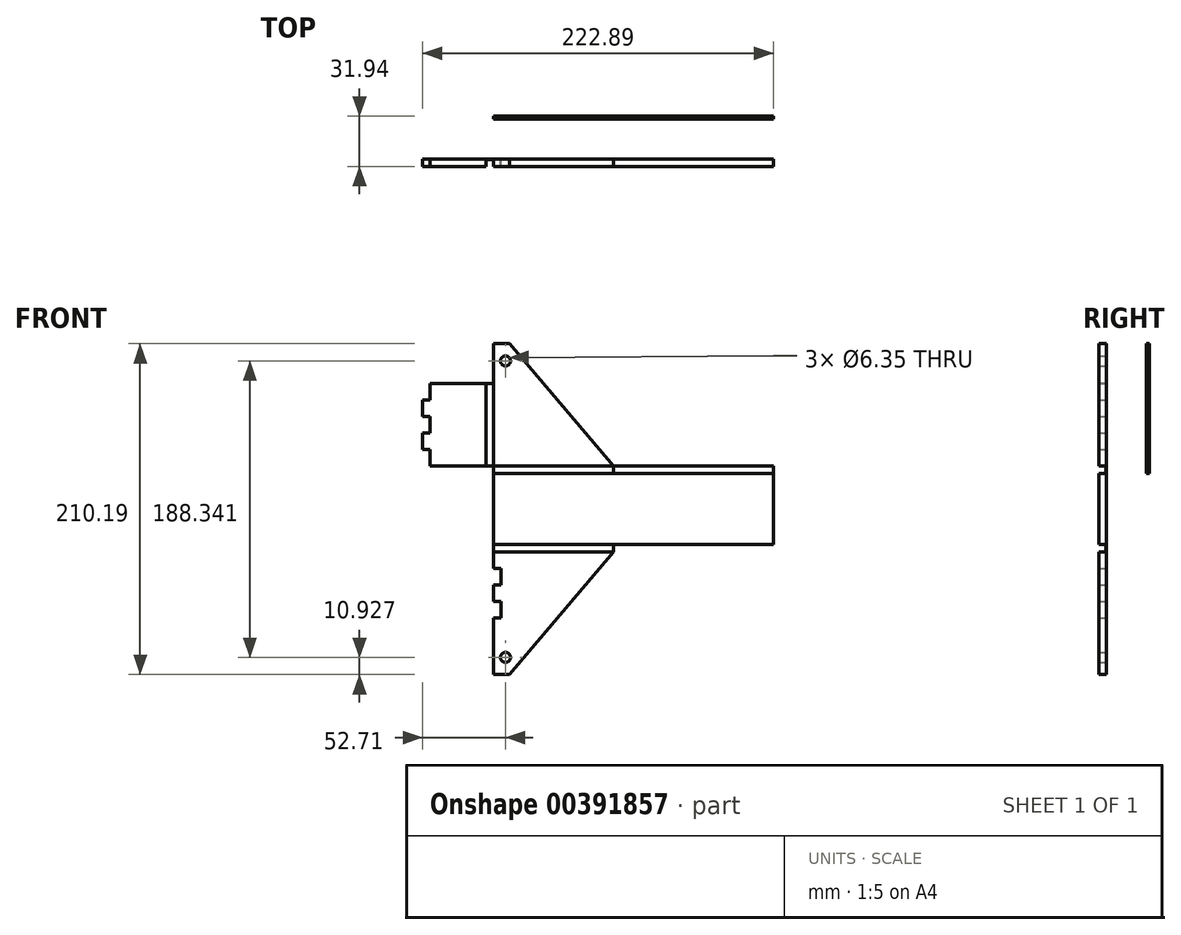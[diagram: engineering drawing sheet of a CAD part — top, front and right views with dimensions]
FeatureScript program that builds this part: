
annotation { "Feature Type Name" : "Feature", "Feature Type Description" : "" }
export const myFeature = defineFeature(function(context is Context, id is Id, definition is map)
    precondition{}
    {
        {
            var Q0;
            Q0=qCreatedBy(makeId("Front.planeOp"),FACE);
            var sketch = newSketch(context, id + "F0", { "sketchPlane" : qUnion([Q0])});
            skLineSegment(sketch, "E0.top", {"start": v(0, 0) * mm, "end": v(177.8, 0) * mm});
            skLineSegment(sketch, "E0.left", {"start": v(0, 82.55) * mm, "end": v(0, 0) * mm});
            skLineSegment(sketch, "E1", {"start": v(177.8, 0) * mm, "end": v(177.8, 4.76) * mm});
            skLineSegment(sketch, "E2", {"start": v(177.8, 4.76) * mm, "end": v(76.2, 4.76) * mm});
            skLineSegment(sketch, "E3", {"start": v(0, 82.55) * mm, "end": v(10.16, 82.55) * mm});
            skLineSegment(sketch, "E4", {"start": v(10.16, 82.55) * mm, "end": v(76.2, 4.76) * mm});
            skSolve(sketch);
        }
        {
            var Q0;
            Q0 = qSketchRegion(id + "F0", true);
            extrude(context, id + "F1", {"entities" : qUnion([Q0]), "depth" : (1.4 + (6 / 16)) * mm});
        }
        {
            var Q0;
            Q0=makeQuery(id+"F1.opExtrude","SWEPT_FACE",FACE,{"disambiguationData":[OSD([sQuery(id+"F0.wireOp",EDGE,"E3")])]});
            var sketch = newSketch(context, id + "F2", { "sketchPlane" : qUnion([Q0])});
            skLineSegment(sketch, "E5.bottom", {"start": v(4.76, -4.76) * mm, "end": v(76.2, -4.76) * mm});
            skLineSegment(sketch, "E5.top", {"start": v(4.76, -40.32) * mm, "end": v(76.2, -40.32) * mm});
            skLineSegment(sketch, "E5.left", {"start": v(4.76, -4.76) * mm, "end": v(4.76, -40.32) * mm});
            skLineSegment(sketch, "E5.right", {"start": v(76.2, -4.76) * mm, "end": v(76.2, -40.32) * mm});
            skSolve(sketch);
        }
        {
            var Q0;
            Q0 = qSketchRegion(id + "F2", true);
            var Q1;
            Q1=makeQuery(id+"F1.opExtrude","SWEPT_FACE",FACE,{"disambiguationData":[OSD([sQuery(id+"F0.wireOp",EDGE,"E2")])]});
            extrude(context, id + "F3", {"entities" : qUnion([Q0]), "operationType" : NewBodyOperationType.REMOVE, "endBound" : BoundingType.UP_TO_SURFACE, "oppositeDirection" : true, "endBoundEntityFace" : qUnion([Q1]), "depth" : 25.4 * mm});
        }
        {
            var Q0;
            Q0=makeQuery(id+"F1.opExtrude","CAP_FACE",FACE,{"disambiguationData":[OSD([sQuery(id+"F0.wireOp",EDGE,"E0.top"),sQuery(id+"F0.wireOp",EDGE,"E0.left"),sQuery(id+"F0.wireOp",EDGE,"E1"),sQuery(id+"F0.wireOp",EDGE,"E2"),sQuery(id+"F0.wireOp",EDGE,"adjmG31n-KMU0-T1bu-X0pq-MTYf4ImsonU8")])],"isStart":false});
            var sketch = newSketch(context, id + "F4", { "sketchPlane" : qUnion([Q0])});
            skCircle(sketch, "E6", {"center": v(7.62, 71.63) * mm, "radius": 3.18 * mm});
            skSolve(sketch);
        }
        {
            var Q0;
            Q0 = qSketchRegion(id + "F4", true);
            extrude(context, id + "F5", {"entities" : qUnion([Q0]), "operationType" : NewBodyOperationType.REMOVE, "endBound" : BoundingType.THROUGH_ALL, "oppositeDirection" : true, "depth" : 25.4 * mm});
        }
        {
            var Q0;
            Q0=makeQuery(id+"F1.opExtrude","SWEPT_FACE",FACE,{"disambiguationData":[OSD([sQuery(id+"F0.wireOp",EDGE,"E0.left")])]});
            var sketch = newSketch(context, id + "F6", { "sketchPlane" : qUnion([Q0])});
            skLineSegment(sketch, "E7.bottom", {"start": v(4.76, 82.55) * mm, "end": v(40.32, 82.55) * mm});
            skLineSegment(sketch, "E7.top", {"start": v(4.76, 57.15) * mm, "end": v(40.32, 57.15) * mm});
            skLineSegment(sketch, "E7.left", {"start": v(4.76, 82.55) * mm, "end": v(4.76, 57.15) * mm});
            skLineSegment(sketch, "E7.right", {"start": v(40.32, 82.55) * mm, "end": v(40.32, 57.15) * mm});
            skSolve(sketch);
        }
        {
            var Q0;
            Q0 = qSketchRegion(id + "F6", true);
            extrude(context, id + "F7", {"entities" : qUnion([Q0]), "operationType" : NewBodyOperationType.REMOVE, "endBound" : BoundingType.THROUGH_ALL, "oppositeDirection" : true, "depth" : 25.4 * mm});
        }
        {
            var Q0;
            Q0=makeQuery(id+"F1.opExtrude","CAP_FACE",FACE,{"disambiguationData":[OSD([sQuery(id+"F0.wireOp",EDGE,"E0.top"),sQuery(id+"F0.wireOp",EDGE,"E0.left"),sQuery(id+"F0.wireOp",EDGE,"E1"),sQuery(id+"F0.wireOp",EDGE,"E2"),sQuery(id+"F0.wireOp",EDGE,"E3"),sQuery(id+"F0.wireOp",EDGE,"E4")])],"isStart":false});
            cPlane(context, id + "F8", {"entities" : qUnion([Q0]), "cplaneType" : CPlaneType.OFFSET, "offset" : 25.4 * mm, "width" : 152.4 * mm, "height" : 152.4 * mm});
        }
        {
            var Q0;
            Q0=qCreatedBy(id+"F8.planeOp",FACE);
            var sketch = newSketch(context, id + "F9", { "sketchPlane" : qUnion([Q0])});
            skLineSegment(sketch, "E8", {"start": v(76.2, 4.76) * mm, "end": v(10.16, 82.55) * mm});
            skLineSegment(sketch, "E9", {"start": v(10.16, 82.55) * mm, "end": v(0, 82.55) * mm});
            skLineSegment(sketch, "E10", {"start": v(76.2, 4.76) * mm, "end": v(0, 4.76) * mm, "construction": true});
            skLineSegment(sketch, "E11", {"start": v(0, 4.76) * mm, "end": v(0, 57.15) * mm, "construction": true});
            skLineSegment(sketch, "E12", {"start": v(76.2, 4.76) * mm, "end": v(76.2, 0) * mm});
            skLineSegment(sketch, "E13", {"start": v(76.2, 0) * mm, "end": v(0, 0) * mm, "construction": true});
            skLineSegment(sketch, "E14", {"start": v(0, 0) * mm, "end": v(0, 4.76) * mm});
            skLineSegment(sketch, "E15", {"start": v(0, 0) * mm, "end": v(0, -45.08) * mm});
            skLineSegment(sketch, "E16", {"start": v(177.8, -45.09) * mm, "end": v(177.8, 0) * mm});
            skLineSegment(sketch, "E17", {"start": v(76.2, 0) * mm, "end": v(177.8, 0) * mm});
            skLineSegment(sketch, "E18", {"start": v(0, -22.54) * mm, "end": v(177.8, -22.54) * mm, "construction": true});
            skLineSegment(sketch, "E19.MirrorCS", {"start": v(76.2, -45.08) * mm, "end": v(177.8, -45.08) * mm});
            skLineSegment(sketch, "E20.MirrorCS", {"start": v(76.2, -45.08) * mm, "end": v(0, -45.08) * mm, "construction": true});
            skLineSegment(sketch, "E21.MirrorCS", {"start": v(0, -45.08) * mm, "end": v(0, -49.85) * mm});
            skLineSegment(sketch, "E22.MirrorCS", {"start": v(76.2, -49.85) * mm, "end": v(0, -49.85) * mm, "construction": true});
            skLineSegment(sketch, "E23.MirrorCS", {"start": v(76.2, -49.85) * mm, "end": v(10.16, -127.64) * mm});
            skLineSegment(sketch, "E24.MirrorCS", {"start": v(76.2, -49.85) * mm, "end": v(76.2, -45.08) * mm});
            skLineSegment(sketch, "E25.MirrorCS", {"start": v(10.16, -127.64) * mm, "end": v(0, -127.64) * mm});
            skLineSegment(sketch, "E26", {"start": v(0, 4.76) * mm, "end": v(-4.76, 4.76) * mm});
            skLineSegment(sketch, "E27", {"start": v(-4.76, 4.76) * mm, "end": v(-4.76, 57.15) * mm, "construction": true});
            skLineSegment(sketch, "E28", {"start": v(-4.76, 57.15) * mm, "end": v(0, 57.15) * mm});
            skLineSegment(sketch, "E29", {"start": v(-4.76, 4.76) * mm, "end": v(-40.32, 4.76) * mm});
            skLineSegment(sketch, "E30", {"start": v(-40.32, 57.15) * mm, "end": v(-4.76, 57.15) * mm});
            skLineSegment(sketch, "E31", {"start": v(-40.32, 4.76) * mm, "end": v(-45.08, 4.76) * mm, "construction": true});
            skLineSegment(sketch, "E32", {"start": v(-45.08, 57.15) * mm, "end": v(-40.32, 57.15) * mm, "construction": true});
            skLineSegment(sketch, "E33", {"start": v(-45.08, 57.15) * mm, "end": v(-45.08, 46.67) * mm, "construction": true});
            skLineSegment(sketch, "E34", {"start": v(-45.08, 46.67) * mm, "end": v(-45.08, 36.2) * mm});
            skLineSegment(sketch, "E35", {"start": v(-45.08, 36.2) * mm, "end": v(-45.08, 25.72) * mm, "construction": true});
            skLineSegment(sketch, "E36", {"start": v(-45.08, 25.72) * mm, "end": v(-45.08, 15.24) * mm});
            skLineSegment(sketch, "E37", {"start": v(-45.08, 15.24) * mm, "end": v(-45.08, 4.76) * mm, "construction": true});
            skLineSegment(sketch, "E38", {"start": v(-45.08, 46.67) * mm, "end": v(-40.32, 46.67) * mm});
            skLineSegment(sketch, "E39", {"start": v(-45.08, 36.2) * mm, "end": v(-40.32, 36.2) * mm});
            skLineSegment(sketch, "E40", {"start": v(-45.08, 25.72) * mm, "end": v(-40.32, 25.72) * mm});
            skLineSegment(sketch, "E41", {"start": v(-45.08, 15.24) * mm, "end": v(-40.32, 15.24) * mm});
            skLineSegment(sketch, "E42", {"start": v(-40.32, 57.15) * mm, "end": v(-40.32, 46.67) * mm});
            skLineSegment(sketch, "E43", {"start": v(-40.32, 36.2) * mm, "end": v(-40.32, 25.72) * mm});
            skLineSegment(sketch, "E44", {"start": v(-40.32, 15.24) * mm, "end": v(-40.32, 4.76) * mm});
            skLineSegment(sketch, "E45", {"start": v(-40.32, 15.24) * mm, "end": v(-40.32, 25.72) * mm, "construction": true});
            skLineSegment(sketch, "E46", {"start": v(-40.32, 36.2) * mm, "end": v(-40.32, 46.67) * mm, "construction": true});
            skLineSegment(sketch, "E47", {"start": v(0, -49.85) * mm, "end": v(0, -60.33) * mm});
            skLineSegment(sketch, "E48", {"start": v(0, -60.33) * mm, "end": v(0, -70.8) * mm, "construction": true});
            skLineSegment(sketch, "E49", {"start": v(0, -81.28) * mm, "end": v(0, -91.76) * mm, "construction": true});
            skLineSegment(sketch, "E50", {"start": v(0, -91.76) * mm, "end": v(0, -102.23) * mm});
            skLineSegment(sketch, "E51", {"start": v(0, -102.23) * mm, "end": v(0, -127.64) * mm});
            skLineSegment(sketch, "E52", {"start": v(0, 57.15) * mm, "end": v(0, 82.55) * mm});
            skLineSegment(sketch, "E53", {"start": v(0, -70.8) * mm, "end": v(0, -81.28) * mm});
            skLineSegment(sketch, "E54", {"start": v(0, -60.33) * mm, "end": v(4.76, -60.33) * mm});
            skLineSegment(sketch, "E55", {"start": v(4.76, -60.33) * mm, "end": v(4.76, -70.8) * mm});
            skLineSegment(sketch, "E56", {"start": v(4.76, -70.8) * mm, "end": v(0, -70.8) * mm});
            skLineSegment(sketch, "E57", {"start": v(0, -81.28) * mm, "end": v(4.76, -81.28) * mm});
            skLineSegment(sketch, "E58", {"start": v(4.76, -81.28) * mm, "end": v(4.76, -91.76) * mm});
            skLineSegment(sketch, "E59", {"start": v(4.76, -91.76) * mm, "end": v(0, -91.76) * mm});
            skCircle(sketch, "E60", {"center": v(7.62, 71.63) * mm, "radius": 3.18 * mm});
            skCircle(sketch, "E61.MirrorC", {"center": v(7.62, -116.71) * mm, "radius": 3.18 * mm});
            skLineSegment(sketch, "E62", {"start": v(-45.08, 51.91) * mm, "end": v(0, 51.91) * mm, "construction": true});
            skSolve(sketch);
        }
        {
            var Q0;
            Q0 = qSketchRegion(id + "F9", true);
            extrude(context, id + "F10", {"entities" : qUnion([Q0]), "depth" : 4.76 * mm});
        }
        {
            var Q0;
            Q0=makeQuery(id+"F10.opExtrude","CAP_FACE",FACE,{"disambiguationData":[OSD([sQuery(id+"F9.wireOp",EDGE,"E8"),sQuery(id+"F9.wireOp",EDGE,"E9"),sQuery(id+"F9.wireOp",EDGE,"E12"),sQuery(id+"F9.wireOp",EDGE,"E14"),sQuery(id+"F9.wireOp",EDGE,"E15"),sQuery(id+"F9.wireOp",EDGE,"E16"),sQuery(id+"F9.wireOp",EDGE,"E17"),sQuery(id+"F9.wireOp",EDGE,"E19.MirrorCS"),sQuery(id+"F9.wireOp",EDGE,"E21.MirrorCS"),sQuery(id+"F9.wireOp",EDGE,"E23.MirrorCS"),sQuery(id+"F9.wireOp",EDGE,"E24.MirrorCS"),sQuery(id+"F9.wireOp",EDGE,"E25.MirrorCS"),sQuery(id+"F9.wireOp",EDGE,"E26"),sQuery(id+"F9.wireOp",EDGE,"E28"),sQuery(id+"F9.wireOp",EDGE,"E29"),sQuery(id+"F9.wireOp",EDGE,"E30"),sQuery(id+"F9.wireOp",EDGE,"E34"),sQuery(id+"F9.wireOp",EDGE,"E36"),sQuery(id+"F9.wireOp",EDGE,"E38"),sQuery(id+"F9.wireOp",EDGE,"E39"),sQuery(id+"F9.wireOp",EDGE,"E40"),sQuery(id+"F9.wireOp",EDGE,"E41"),sQuery(id+"F9.wireOp",EDGE,"E42"),sQuery(id+"F9.wireOp",EDGE,"E43"),sQuery(id+"F9.wireOp",EDGE,"E44"),sQuery(id+"F9.wireOp",EDGE,"E47"),sQuery(id+"F9.wireOp",EDGE,"E50"),sQuery(id+"F9.wireOp",EDGE,"E51"),sQuery(id+"F9.wireOp",EDGE,"E52"),sQuery(id+"F9.wireOp",EDGE,"E53"),sQuery(id+"F9.wireOp",EDGE,"E54"),sQuery(id+"F9.wireOp",EDGE,"E55"),sQuery(id+"F9.wireOp",EDGE,"E56"),sQuery(id+"F9.wireOp",EDGE,"E57"),sQuery(id+"F9.wireOp",EDGE,"E58"),sQuery(id+"F9.wireOp",EDGE,"E59")])],"isStart":false});
            var sketch = newSketch(context, id + "F11", { "sketchPlane" : qUnion([Q0])});
            skLineSegment(sketch, "E63.bottom", {"start": v(0, 4.76) * mm, "end": v(-4.76, 4.76) * mm});
            skLineSegment(sketch, "E63.top", {"start": v(0, 57.15) * mm, "end": v(-4.76, 57.15) * mm});
            skLineSegment(sketch, "E63.left", {"start": v(0, 4.76) * mm, "end": v(0, 57.15) * mm});
            skLineSegment(sketch, "E63.right", {"start": v(-4.76, 4.76) * mm, "end": v(-4.76, 57.15) * mm});
            skLineSegment(sketch, "E64.bottom", {"start": v(0, 4.76) * mm, "end": v(76.2, 4.76) * mm});
            skLineSegment(sketch, "E64.top", {"start": v(0, 0) * mm, "end": v(76.2, 0) * mm});
            skLineSegment(sketch, "E64.left", {"start": v(0, 4.76) * mm, "end": v(0, 0) * mm});
            skLineSegment(sketch, "E64.right", {"start": v(76.2, 4.76) * mm, "end": v(76.2, 0) * mm});
            skLineSegment(sketch, "E65.bottom", {"start": v(76.2, -49.85) * mm, "end": v(0, -49.85) * mm});
            skLineSegment(sketch, "E65.top", {"start": v(76.2, -45.08) * mm, "end": v(0, -45.08) * mm});
            skLineSegment(sketch, "E65.left", {"start": v(76.2, -49.85) * mm, "end": v(76.2, -45.08) * mm});
            skLineSegment(sketch, "E65.right", {"start": v(0, -49.85) * mm, "end": v(0, -45.08) * mm});
            skSolve(sketch);
        }
        {
            var Q0;
            Q0 = qSketchRegion(id + "F11", true);
            extrude(context, id + "F12", {"entities" : qUnion([Q0]), "operationType" : NewBodyOperationType.REMOVE, "oppositeDirection" : true, "depth" : 4.5 * mm});
        }
    });
